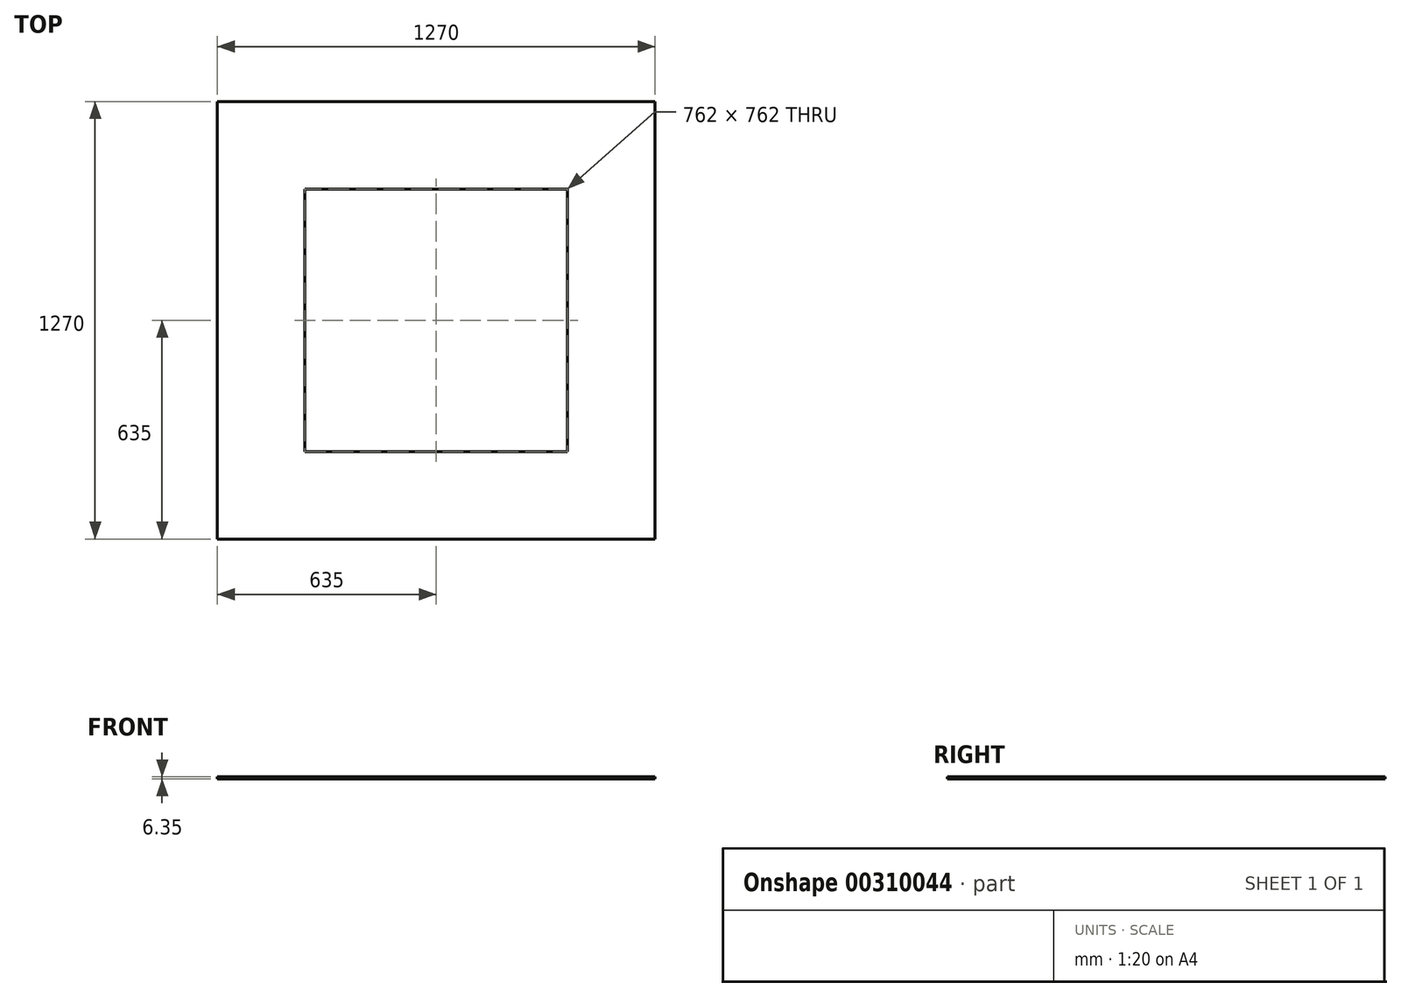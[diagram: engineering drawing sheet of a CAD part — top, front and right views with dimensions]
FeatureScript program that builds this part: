
annotation { "Feature Type Name" : "Feature", "Feature Type Description" : "" }
export const myFeature = defineFeature(function(context is Context, id is Id, definition is map)
    precondition{}
    {
        {
            var Q0;
            Q0=qCreatedBy(makeId("Top.planeOp"),FACE);
            var sketch = newSketch(context, id + "F0", { "sketchPlane" : qUnion([Q0])});
            skLineSegment(sketch, "E0.bottom", {"start": v(635, 635) * mm, "end": v(-635, 635) * mm});
            skLineSegment(sketch, "E0.top", {"start": v(635, -635) * mm, "end": v(-635, -635) * mm});
            skLineSegment(sketch, "E0.left", {"start": v(635, 635) * mm, "end": v(635, -635) * mm});
            skLineSegment(sketch, "E0.right", {"start": v(-635, 635) * mm, "end": v(-635, -635) * mm});
            skPoint(sketch, "E0.middle", {"position": v(0, 0) * mm});
            skLineSegment(sketch, "E1.bottom", {"start": v(381, 381) * mm, "end": v(-381, 381) * mm});
            skLineSegment(sketch, "E1.top", {"start": v(381, -381) * mm, "end": v(-381, -381) * mm});
            skLineSegment(sketch, "E1.left", {"start": v(381, 381) * mm, "end": v(381, -381) * mm});
            skLineSegment(sketch, "E1.right", {"start": v(-381, 381) * mm, "end": v(-381, -381) * mm});
            skSolve(sketch);
        }
        {
            var Q0;
            Q0=makeQuery(id+"F0.imprint","IMPRINT",FACE,{"disambiguationData":[TD([[makeQuery(id+"F0.imprint","IMPRINT",EDGE,{"derivedFrom":sQuery(id+"F0.wireOp",EDGE,"E0.bottom")}),1.0]])]});
            extrude(context, id + "F1", {"entities" : qUnion([Q0]), "depth" : 6.35 * mm, "offsetDistance" : 25.4 * mm});
        }
    });
